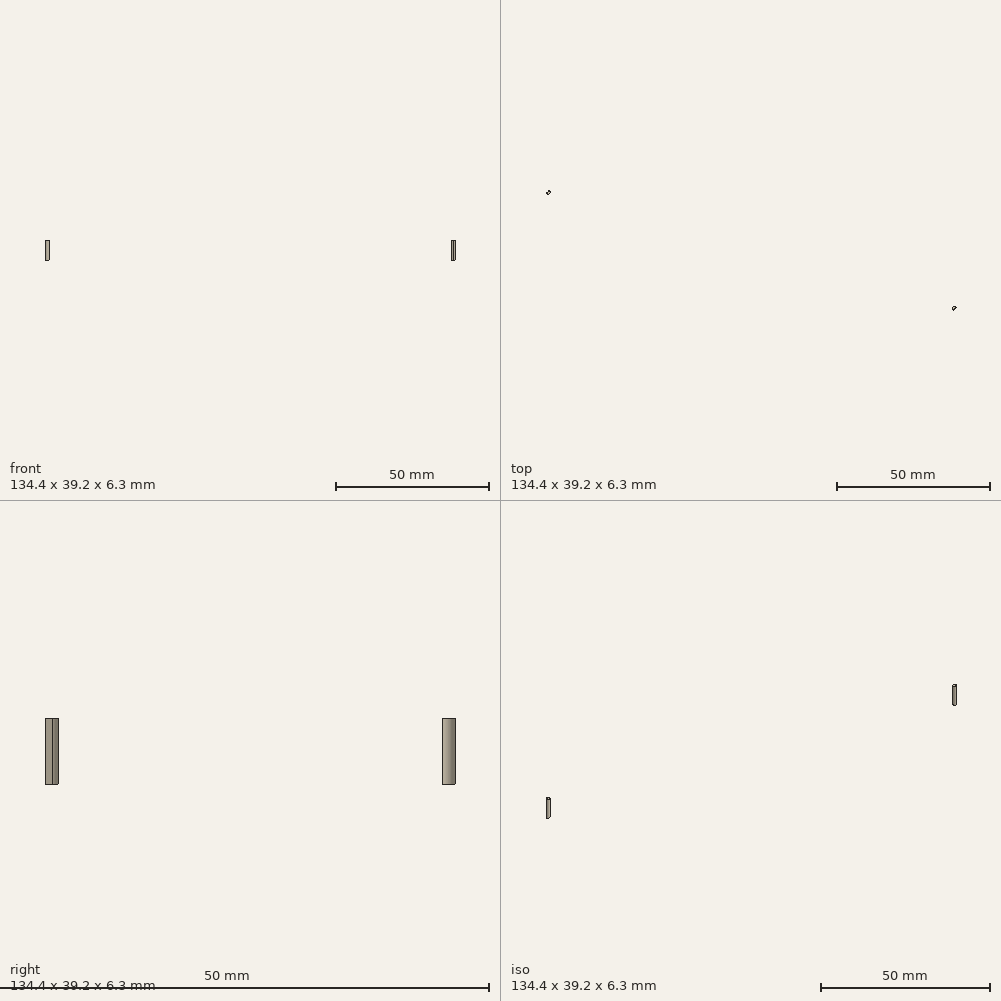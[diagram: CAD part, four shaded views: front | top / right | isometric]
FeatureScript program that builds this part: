
annotation { "Feature Type Name" : "Feature", "Feature Type Description" : "" }
export const myFeature = defineFeature(function(context is Context, id is Id, definition is map)
    precondition{}
    {
        {
            var Q0;
            Q0=qCreatedBy(makeId("Top.planeOp"),FACE);
            var sketch = newSketch(context, id + "F0", { "sketchPlane" : qUnion([Q0])});
            skLineSegment(sketch, "E0.bottom", {"start": v(66.55, -50.8) * mm, "end": v(-66.55, -50.8) * mm});
            skLineSegment(sketch, "E0.top", {"start": v(66.55, 50.8) * mm, "end": v(-66.55, 50.8) * mm});
            skLineSegment(sketch, "E0.left", {"start": v(66.55, -50.8) * mm, "end": v(66.55, 50.8) * mm});
            skLineSegment(sketch, "E0.right", {"start": v(-66.55, -50.8) * mm, "end": v(-66.55, 50.8) * mm});
            skPoint(sketch, "E0.middle", {"position": v(0, 0) * mm});
            skSolve(sketch);
        }
        {
            var Q0;
            Q0=qSketchRegion(id+"F0",true);
            extrude(context, id + "F1", {"entities" : qUnion([Q0]), "depth" : 6.35 * mm, "offsetDistance" : 25.4 * mm});
        }
        {
            var Q0;
            Q0=makeQuery(id+"F1.opExtrude","CAP_FACE",FACE,{"disambiguationData":[OSD([sQuery(id+"F0.wireOp",EDGE,"E0.bottom"),sQuery(id+"F0.wireOp",EDGE,"E0.top"),sQuery(id+"F0.wireOp",EDGE,"E0.left"),sQuery(id+"F0.wireOp",EDGE,"E0.right")])],"isStart":false});
            var sketch = newSketch(context, id + "F2", { "sketchPlane" : qUnion([Q0])});
            skLineSegment(sketch, "E1.bottom", {"start": v(-73.03, 18.99) * mm, "end": v(-66.55, 18.99) * mm});
            skLineSegment(sketch, "E1.top", {"start": v(-73.03, -18.99) * mm, "end": v(-66.55, -18.99) * mm});
            skLineSegment(sketch, "E1.left", {"start": v(-66.55, 18.99) * mm, "end": v(-66.55, -18.99) * mm});
            skLineSegment(sketch, "E1.right", {"start": v(-73.02, 18.99) * mm, "end": v(-73.02, -18.99) * mm});
            skLineSegment(sketch, "E2.bottom", {"start": v(73.02, 18.99) * mm, "end": v(66.55, 18.99) * mm});
            skLineSegment(sketch, "E2.top", {"start": v(73.02, -18.99) * mm, "end": v(66.55, -18.99) * mm});
            skLineSegment(sketch, "E2.left", {"start": v(66.55, 18.99) * mm, "end": v(66.55, -18.99) * mm});
            skLineSegment(sketch, "E2.right", {"start": v(73.03, 18.99) * mm, "end": v(73.03, -18.99) * mm});
            skLineSegment(sketch, "E3", {"start": v(-66.55, 0) * mm, "end": v(66.55, 0) * mm, "construction": true});
            skSolve(sketch);
        }
        {
            var Q0;
            Q0=qSketchRegion(id+"F2",true);
            extrude(context, id + "F3", {"entities" : qUnion([Q0]), "operationType" : NewBodyOperationType.ADD, "oppositeDirection" : true, "depth" : 6.35 * mm, "offsetDistance" : 25.4 * mm});
        }
        {
            var Q0;
            Q0=makeQuery(id+"F1.opExtrude","CAP_FACE",FACE,{"disambiguationData":[OSD([sQuery(id+"F0.wireOp",EDGE,"E0.bottom"),sQuery(id+"F0.wireOp",EDGE,"E0.top"),sQuery(id+"F0.wireOp",EDGE,"E0.left"),sQuery(id+"F0.wireOp",EDGE,"E0.right")])],"isStart":false});
            var sketch = newSketch(context, id + "F4", { "sketchPlane" : qUnion([Q0])});
            skLineSegment(sketch, "E4.bottom", {"start": v(-63.5, 42.86) * mm, "end": v(63.5, 42.86) * mm});
            skLineSegment(sketch, "E4.top", {"start": v(-63.5, 7.94) * mm, "end": v(63.5, 7.94) * mm});
            skLineSegment(sketch, "E4.left", {"start": v(-63.5, 42.86) * mm, "end": v(-63.5, 7.94) * mm});
            skLineSegment(sketch, "E4.right", {"start": v(63.5, 42.86) * mm, "end": v(63.5, 7.94) * mm});
            skLineSegment(sketch, "E5.bottom", {"start": v(-63.5, 4.76) * mm, "end": v(63.5, 4.76) * mm});
            skLineSegment(sketch, "E5.top", {"start": v(-63.5, -46.04) * mm, "end": v(63.5, -46.04) * mm});
            skLineSegment(sketch, "E5.left", {"start": v(-63.5, 4.76) * mm, "end": v(-63.5, -46.04) * mm});
            skLineSegment(sketch, "E5.right", {"start": v(63.5, 4.76) * mm, "end": v(63.5, -46.04) * mm});
            skPoint(sketch, "E6", {"position": v(0, 42.86) * mm});
            skSolve(sketch);
        }
        {
            var Q0;
            Q0=qSketchRegion(id+"F4",true);
            extrude(context, id + "F5", {"entities" : qUnion([Q0]), "operationType" : NewBodyOperationType.ADD, "depth" : 3.17 * mm, "offsetDistance" : 25.4 * mm});
        }
        {
            var Q0;
            Q0=makeQuery(id+"F3.boolean.opBoolean","MERGE",FACE,{"derivedFrom":[makeQuery(id+"F1.opExtrude","CAP_FACE",FACE,{"disambiguationData":[OSD([sQuery(id+"F0.wireOp",EDGE,"E0.bottom"),sQuery(id+"F0.wireOp",EDGE,"E0.top"),sQuery(id+"F0.wireOp",EDGE,"E0.left"),sQuery(id+"F0.wireOp",EDGE,"E0.right")])],"isStart":true}),makeQuery(id+"F3.opExtrude","CAP_FACE",FACE,{"disambiguationData":[OSD([sQuery(id+"F2.wireOp",EDGE,"E1.bottom"),sQuery(id+"F2.wireOp",EDGE,"E1.top"),sQuery(id+"F2.wireOp",EDGE,"E1.left"),sQuery(id+"F2.wireOp",EDGE,"E1.right")])],"isStart":false}),makeQuery(id+"F3.opExtrude","CAP_FACE",FACE,{"disambiguationData":[OSD([sQuery(id+"F2.wireOp",EDGE,"E2.bottom"),sQuery(id+"F2.wireOp",EDGE,"E2.top"),sQuery(id+"F2.wireOp",EDGE,"E2.left"),sQuery(id+"F2.wireOp",EDGE,"E2.right")])],"isStart":false})]});
            var sketch = newSketch(context, id + "F6", { "sketchPlane" : qUnion([Q0])});
            skArc(sketch, "E7", {"start": v(-67.18, 18.99) * mm, "mid": v(-66.1, 18.54) * mm, "end": v(-66.55, 19.62) * mm});
            skArc(sketch, "E8", {"start": v(-67.18, -18.99) * mm, "mid": v(-66.1, -18.54) * mm, "end": v(-66.55, -19.62) * mm});
            skArc(sketch, "E9", {"start": v(67.18, -18.99) * mm, "mid": v(66.1, -18.54) * mm, "end": v(66.55, -19.62) * mm});
            skArc(sketch, "E10", {"start": v(67.18, 18.99) * mm, "mid": v(66.1, 18.54) * mm, "end": v(66.55, 19.62) * mm});
            skLineSegment(sketch, "E11", {"start": v(66.55, 18.99) * mm, "end": v(66.55, 19.62) * mm});
            skLineSegment(sketch, "E12", {"start": v(66.55, 18.99) * mm, "end": v(67.18, 18.99) * mm});
            skLineSegment(sketch, "E13", {"start": v(66.55, -18.99) * mm, "end": v(67.18, -18.99) * mm});
            skLineSegment(sketch, "E14", {"start": v(66.55, -18.99) * mm, "end": v(66.55, -19.62) * mm});
            skLineSegment(sketch, "E15", {"start": v(-66.55, -18.99) * mm, "end": v(-66.55, -19.62) * mm});
            skLineSegment(sketch, "E16", {"start": v(-66.55, 18.99) * mm, "end": v(-66.55, 19.62) * mm});
            skLineSegment(sketch, "E17", {"start": v(-66.55, 18.99) * mm, "end": v(-67.18, 18.99) * mm});
            skLineSegment(sketch, "E18", {"start": v(-66.55, -18.99) * mm, "end": v(-67.18, -18.99) * mm});
            skSolve(sketch);
        }
        {
            var Q0;
            Q0=makeQuery(id+"F6.imprint","IMPRINT",FACE,{"disambiguationData":[TD([[makeQuery(id+"F6.imprint","IMPRINT",EDGE,{"derivedFrom":sQuery(id+"F6.wireOp",EDGE,"E8")}),-1.0]])]});
            var Q1;
            Q1=makeQuery(id+"F6.imprint","IMPRINT",FACE,{"disambiguationData":[TD([[makeQuery(id+"F6.imprint","IMPRINT",EDGE,{"derivedFrom":sQuery(id+"F6.wireOp",EDGE,"E7")}),1.0]])]});
            var Q2;
            Q2=makeQuery(id+"F6.imprint","IMPRINT",FACE,{"disambiguationData":[TD([[makeQuery(id+"F6.imprint","IMPRINT",EDGE,{"derivedFrom":sQuery(id+"F6.wireOp",EDGE,"E9")}),1.0]])]});
            var Q3;
            Q3=makeQuery(id+"F6.imprint","IMPRINT",FACE,{"disambiguationData":[TD([[makeQuery(id+"F6.imprint","IMPRINT",EDGE,{"derivedFrom":sQuery(id+"F6.wireOp",EDGE,"E10")}),-1.0]])]});
            extrude(context, id + "F7", {"entities" : qUnion([Q0, Q1, Q2, Q3]), "operationType" : NewBodyOperationType.REMOVE, "endBound" : BoundingType.THROUGH_ALL, "oppositeDirection" : true, "depth" : 25.4 * mm, "offsetDistance" : 25.4 * mm});
        }
    });
